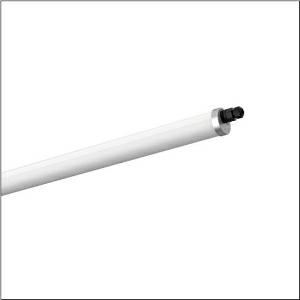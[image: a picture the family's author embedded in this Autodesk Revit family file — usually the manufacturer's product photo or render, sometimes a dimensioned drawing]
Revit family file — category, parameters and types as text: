
# Revit family: monsun_31_tube_51ft10dn4a0a
name_source: partatom
category: Lighting Fixtures
units: mm (PartAtom-declared; Revit-internal decimal feet)

## family parameters
Cut with Voids When Loaded = No
Host = Face
Light Source = No
Part Type = Normal
Room Calculation Point = No
Round Connector Dimension = Use Diameter
Shared = No

## types (1)
- Monsun 31 Tube (1 x LED, 10000 lm, 58 W, 4000K)
    Apparent Load = 58 VA
    CIE Flux Codes = 42 71 90 91 100
    Color Rendering = 80
    Color Temperature = 4000K
    Default Elevation = 1800 mm
    Description = Monsun 31 Tube, tubular luminaire, primary optical cover: diffuser, of PMMA, light emission: direct distribution, primary light characteristic: symmetric, installation type: suspended mounting, surface-mounted, LED, rated luminous flux: 10.000lm, luminous efficacy: 160lm/W, light colour: 840, colour temperature: 4000K, control gear: DALI 2, with with 1 terminal, 5-pole, max. 2.5mm², through-wiring: 5x 1.5mm², mains connection: 220..240V, AC, 50/60Hz, rated input power: 58W, housing, cylindrical, of PMMA, semi-transparent, matt white, with luminaire and ceiling fastening, V4A, mounting with brackets of stainless steel, length: 1.570mm, diameter: 75mm, end cap, of stainless steel (V4A), protection rating (complete): IP67/IP69K, insulation class (complete): insulation class I (protective earthing), certification: CE, UKCA, impact resistance: IK07, permissible operating ambient temperature: -20..+40°C, corresponds to IFS (International Featured Standards) requirements for safety and quality in the food industry, usage in unprotected outdoor areas possible with horizontal mounting, contact your sales advisor before using the luminaires in applications with unclear chemical exposure, large temperature fluctuations or condensation-forming humidity, packaging unit: 1 piece
    Height = 83 mm
    Lamp = 1 x LED
    Lamp Light Flux = 10000 lm
    Lamp Power = 58 W
    Lamp count = 1
    Length = 1570 mm
    Luminous efficacy = 172 lm/W
    Manufacturer = Siteco
    ModVariant = No
    Model = 51FT10DN4A0A
    Mounting Place = Ceiling
    Mounting Type = Pendant
    Number of Poles = 1
    OnlyDefault = Yes
    Power Factor = 1
    Product Name = Monsun 31 Tube
    Product group = tubular luminaire
    ProductGroupID = 906
    Protection Class = Protection class I
    RLX_Detail_Level = 1
    RLX_Emergency_Light_Flux = 0 lm
    RLX_Emergency_Type = 0
    RLX_Emergency_Type_DB = No
    RlxData = <blob elided: 25333 chars, md5=ec66921f>
    Socket = socket
    Standby Power = 0 W
    System Light Flux = 10000 lm
    System Power = 58 W
    Type Comments = Product without accessories
    Type Image = l_1228461.jpg
    URL = http://relux.com
    VarID = ---
    Voltage = 0 V
    Weight = 0.00 kg
    Width = 75 mm

## geometry (parser evidence)
native form markers: Blend x4, Sweep x15
no freeform markers — native parametric forms only
